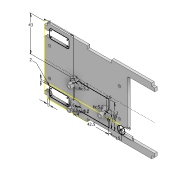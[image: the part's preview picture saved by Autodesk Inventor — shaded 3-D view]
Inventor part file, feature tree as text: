
AUTODESK INVENTOR PART (.ipt)
format: ipt  version: 2022 (Build 260153000, 153)  size: 331,776 bytes
history: native  units: mm
features: extrude x8, sketch x5, fillet x2
ambient origin geometry x8: Origin, YZ Plane, XZ Plane, XY Plane, X Axis, Y Axis, Z Axis, Center Point
bodies: Solid1 (feature_tree)
feature tree (15):
  extrude  "Base Plate"  Depth=80.0mm
  sketch  "Sketch2"  dims[d2=3.5mm d3=3.5mm]
  extrude  "CubePilot Outline"  Depth=3.5mm
  extrude  "Extrusion3"  Depth=3.5mm
  sketch  "Sketch3"  dims[d4=3.5mm d5=3.5mm]
  extrude  "Extrusion4"  Depth=49.0mm
  fillet  "Fillet1"  Radius=3.5mm
  extrude  "Extrusion5"  Depth=3.0mm TaperAngle=0.0deg
  extrude  "Extrusion6"  Depth=44.29mm
  extrude  "Extrusion7"  TaperAngle=0.0deg  [1 undecoded]
  extrude  "Extrusion8"  Depth=94.46mm
  fillet  "Fillet2"  Radius=2.0mm
  sketch  "Sketch1"  dims[d0=134.5mm d1=80.0mm]
  sketch  "Sketch4"  dims[d6=49.0mm d7=49.0mm d8=3.5mm]
  sketch  "Sketch6"  dims[d9=3.5mm d10=3.0mm d11=0.0mm d12=44.29mm d13=0.0mm d14=94.46mm d15=2.0mm d16=4.0mm d17=1.0mm d18=2.8mm d19=20.0mm d21=85.0mm d22=20.0mm d24=34.4mm d27=4.73mm d28=4.945mm d29=0.5mm d30=0.0mm d31=0.0mm d32=0.0mm d33=42.5mm d34=30.0mm d35=43.0mm d36=36.0mm d37=3.2mm d38=3.2mm d39=3.2mm d40=2.5mm d41=2.5mm d42=2.5mm d43=2.5mm d44=2.6mm d45=15.0mm d46=9.0mm d47=5.0mm d48=15.0mm d49=3.0mm d50=4.0mm d51=2.0mm d52=6.0mm d53=2.0mm d54=5.2mm d55=5.2mm d56=5.2mm d57=8.5mm d58=0.0mm d59=4.0mm d60=5.8mm d61=5.8mm d62=5.8mm d63=2.8mm d64=0.0mm d65=0.0mm d66=0.0mm d67=7.5mm d68=7.5mm d69=0.0mm d70=4.0mm d71=2.0mm d72=0.0mm d73=0.0mm d74=12.0mm d75=5.0mm d76=15.0mm d77=15.0mm d78=6.0mm d79=8.0mm d80=2.0mm d81=8.0mm d82=2.0mm d83=0.0mm d84=0.0mm d85=2.0mm]
note: 1 required parameter value undecoded (feature->parameter linkage not recoverable at this tier; creation-order binding heuristic only, values carry confidence <= 0.55)
